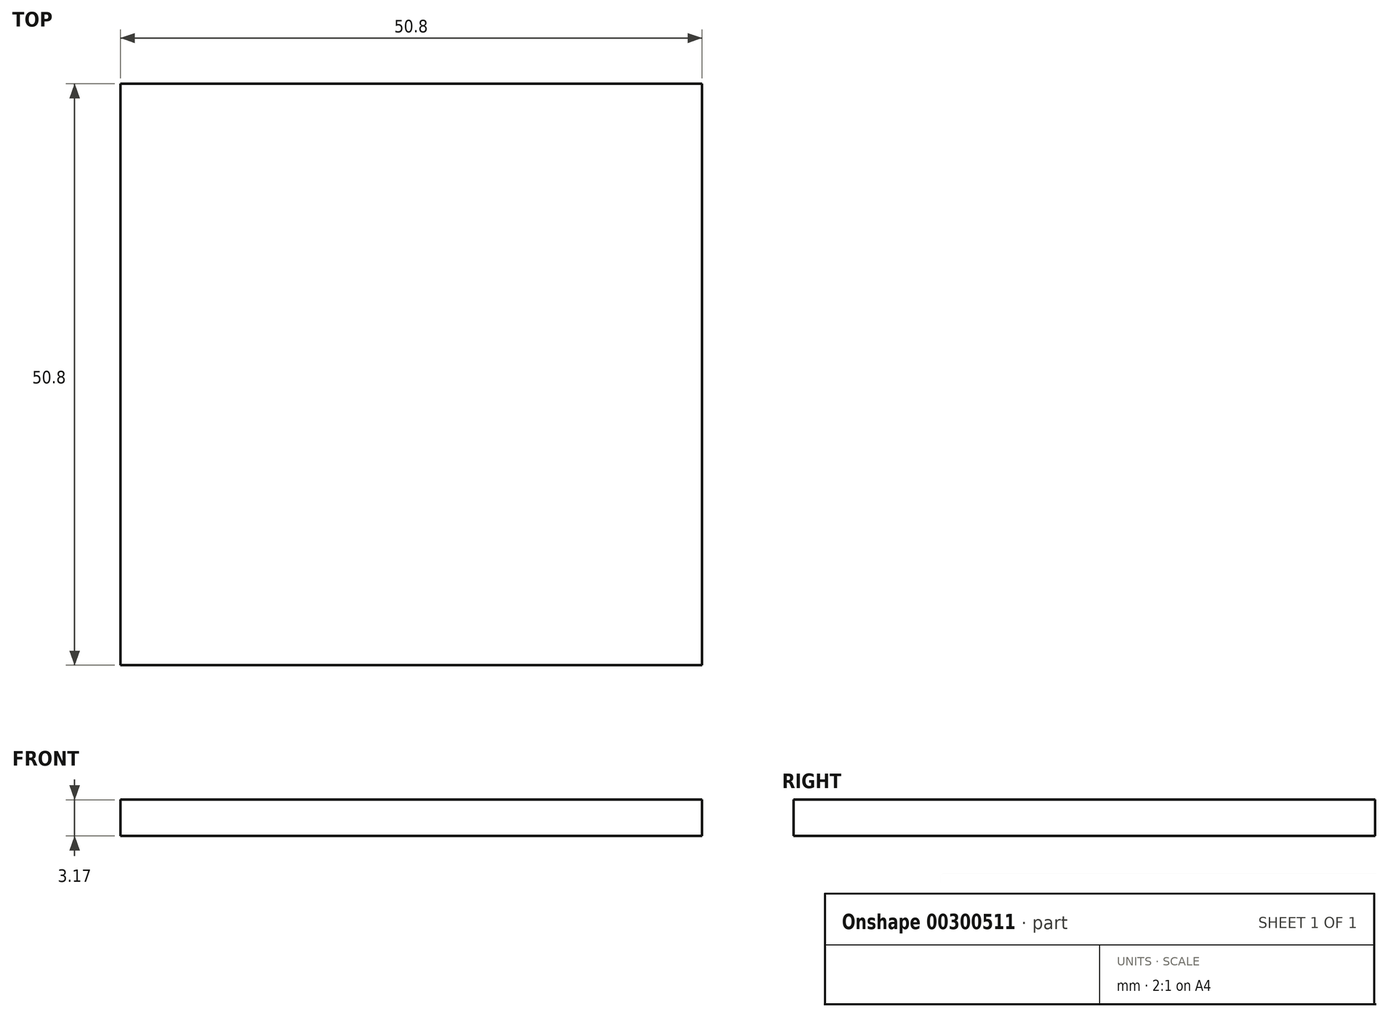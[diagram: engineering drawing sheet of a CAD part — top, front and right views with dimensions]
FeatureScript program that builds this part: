
annotation { "Feature Type Name" : "Feature", "Feature Type Description" : "" }
export const myFeature = defineFeature(function(context is Context, id is Id, definition is map)
    precondition{}
    {
        {
            var Q0;
            Q0=qCreatedBy(makeId("Top.planeOp"),FACE);
            var sketch = newSketch(context, id + "F0", { "sketchPlane" : qUnion([Q0])});
            skLineSegment(sketch, "E0.bottom", {"start": v(-25.4, -25.4) * mm, "end": v(25.4, -25.4) * mm});
            skLineSegment(sketch, "E0.top", {"start": v(-25.4, 25.4) * mm, "end": v(25.4, 25.4) * mm});
            skLineSegment(sketch, "E0.left", {"start": v(-25.4, -25.4) * mm, "end": v(-25.4, 25.4) * mm});
            skLineSegment(sketch, "E0.right", {"start": v(25.4, -25.4) * mm, "end": v(25.4, 25.4) * mm});
            skPoint(sketch, "E0.middle", {"position": v(0, 0) * mm});
            skSolve(sketch);
        }
        {
            var Q0;
            Q0 = qSketchRegion(id + "F0", true);
            extrude(context, id + "F1", {"entities" : qUnion([Q0]), "depth" : 3.17 * mm});
        }
    });
